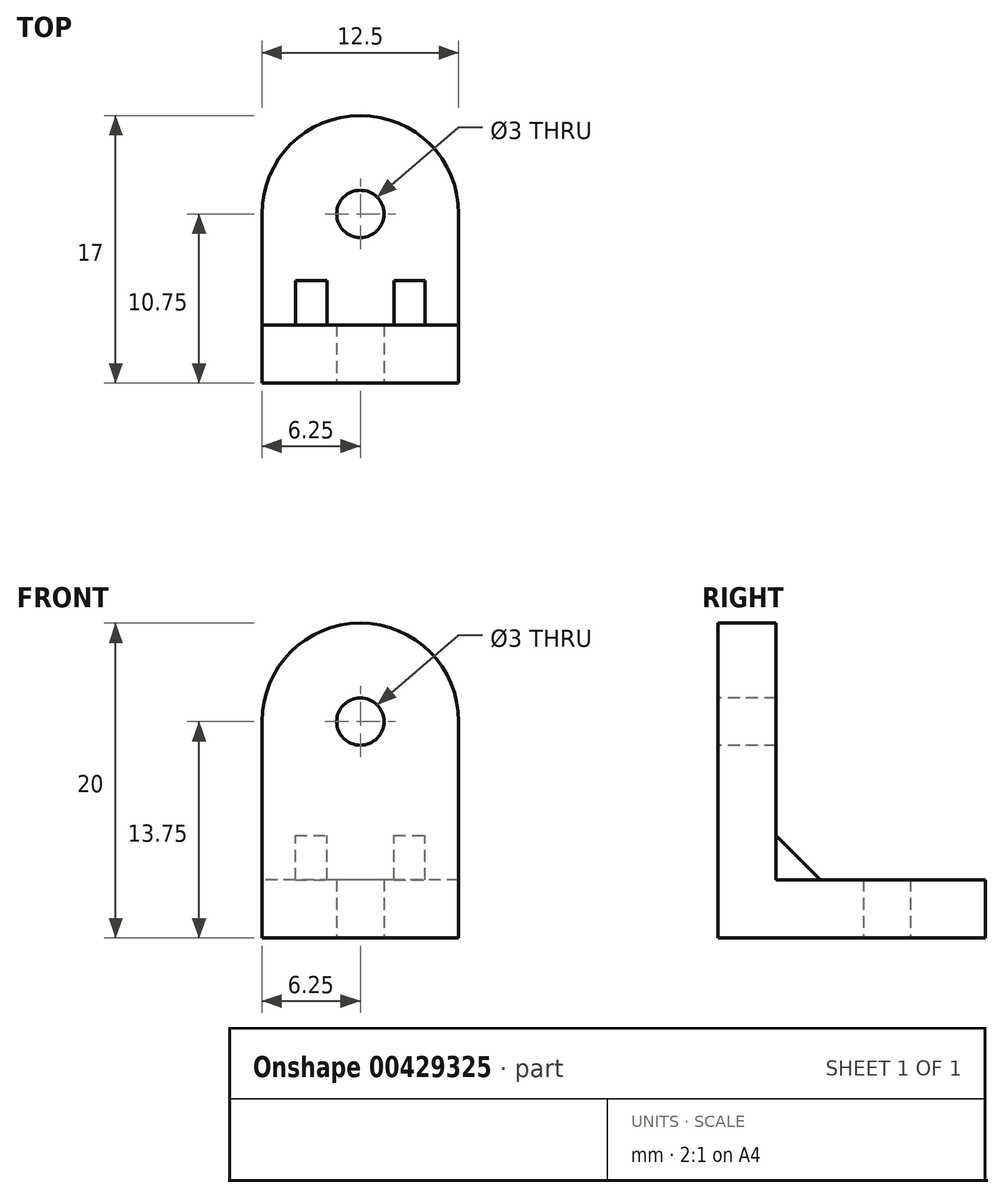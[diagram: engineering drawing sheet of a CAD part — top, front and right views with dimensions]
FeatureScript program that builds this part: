
annotation { "Feature Type Name" : "Feature", "Feature Type Description" : "" }
export const myFeature = defineFeature(function(context is Context, id is Id, definition is map)
    precondition{}
    {
        {
            var Q0;
            Q0=qCreatedBy(makeId("Front.planeOp"),FACE);
            var sketch = newSketch(context, id + "F0", { "sketchPlane" : qUnion([Q0])});
            skLineSegment(sketch, "E0.bottom", {"start": v(0, 0) * mm, "end": v(12.5, 0) * mm});
            skLineSegment(sketch, "E0.top", {"start": v(6.25, 20) * mm, "end": v(6.25, 20) * mm});
            skLineSegment(sketch, "E0.left", {"start": v(0, 0) * mm, "end": v(0, 13.75) * mm});
            skLineSegment(sketch, "E0.right", {"start": v(12.5, 0) * mm, "end": v(12.5, 13.75) * mm});
            skPoint(sketch, "E1.visualSharp", {"position": v(0, 20) * mm});
            skArc(sketch, "E1.filletArc", {"start": v(6.25, 20) * mm, "mid": v(1.83, 18.17) * mm, "end": v(0, 13.75) * mm});
            skPoint(sketch, "E2.visualSharp", {"position": v(12.5, 20) * mm});
            skArc(sketch, "E2.filletArc", {"start": v(12.5, 13.75) * mm, "mid": v(10.67, 18.17) * mm, "end": v(6.25, 20) * mm});
            skCircle(sketch, "E3", {"center": v(6.25, 13.75) * mm, "radius": 1.5 * mm});
            skSolve(sketch);
        }
        {
            var Q0;
            Q0=qCreatedBy(makeId("Top.planeOp"),FACE);
            var sketch = newSketch(context, id + "F1", { "sketchPlane" : qUnion([Q0])});
            skLineSegment(sketch, "E4.bottom", {"start": v(0, 0) * mm, "end": v(12.5, 0) * mm});
            skLineSegment(sketch, "E4.top", {"start": v(6.25, 17) * mm, "end": v(6.25, 17) * mm});
            skLineSegment(sketch, "E4.left", {"start": v(0, 0) * mm, "end": v(0, 10.75) * mm});
            skLineSegment(sketch, "E4.right", {"start": v(12.5, 0) * mm, "end": v(12.5, 10.75) * mm});
            skPoint(sketch, "E5.visualSharp", {"position": v(0, 17) * mm});
            skArc(sketch, "E5.filletArc", {"start": v(6.25, 17) * mm, "mid": v(1.83, 15.17) * mm, "end": v(0, 10.75) * mm});
            skPoint(sketch, "E6.visualSharp", {"position": v(12.5, 17) * mm});
            skArc(sketch, "E6.filletArc", {"start": v(12.5, 10.75) * mm, "mid": v(10.67, 15.17) * mm, "end": v(6.25, 17) * mm});
            skCircle(sketch, "E7", {"center": v(6.25, 10.75) * mm, "radius": 1.5 * mm});
            skSolve(sketch);
        }
        {
            var Q0;
            Q0=makeQuery(id+"F0.imprint","IMPRINT",FACE,{"disambiguationData":[TD([[makeQuery(id+"F0.imprint","IMPRINT",EDGE,{"derivedFrom":sQuery(id+"F0.wireOp",EDGE,"E0.bottom")}),1.0]])]});
            extrude(context, id + "F2", {"entities" : qUnion([Q0]), "oppositeDirection" : true, "depth" : 3.7 * mm});
        }
        {
            var Q0;
            Q0=makeQuery(id+"F1.imprint","IMPRINT",FACE,{"disambiguationData":[TD([[makeQuery(id+"F1.imprint","IMPRINT",EDGE,{"derivedFrom":sQuery(id+"F1.wireOp",EDGE,"E4.bottom")}),1.0]])]});
            extrude(context, id + "F3", {"entities" : qUnion([Q0]), "operationType" : NewBodyOperationType.ADD, "depth" : 3.7 * mm});
        }
        {
            var Q0;
            Q0=makeQuery(id+"F3.boolean.opBoolean","INTERSECT",EDGE,{"derivedFrom":[makeQuery(id+"F2.opExtrude","CAP_FACE",FACE,{"disambiguationData":[OSD([sQuery(id+"F0.wireOp",EDGE,"E0.bottom"),sQuery(id+"F0.wireOp",EDGE,"E0.left"),sQuery(id+"F0.wireOp",EDGE,"E0.right"),sQuery(id+"F0.wireOp",EDGE,"E1.filletArc"),sQuery(id+"F0.wireOp",EDGE,"E2.filletArc"),sQuery(id+"F0.wireOp",EDGE,"E3")])],"isStart":false}),makeQuery(id+"F3.opExtrude","CAP_FACE",FACE,{"disambiguationData":[OSD([sQuery(id+"F1.wireOp",EDGE,"E4.bottom"),sQuery(id+"F1.wireOp",EDGE,"E4.left"),sQuery(id+"F1.wireOp",EDGE,"E4.right"),sQuery(id+"F1.wireOp",EDGE,"E5.filletArc"),sQuery(id+"F1.wireOp",EDGE,"E6.filletArc"),sQuery(id+"F1.wireOp",EDGE,"E7")])],"isStart":false})]});
            cPlane(context, id + "F4", {"entities" : qUnion([Q0]), "cplaneType" : CPlaneType.LINE_ANGLE, "offset" : 25 * mm, "angle" : 45 * degree, "oppositeDirection" : true, "width" : 150 * mm, "height" : 150 * mm});
        }
        {
            var Q0;
            Q0=qCreatedBy(id+"F4.planeOp",FACE);
            cPlane(context, id + "F5", {"entities" : qUnion([Q0]), "cplaneType" : CPlaneType.OFFSET, "offset" : 2 * mm, "oppositeDirection" : true, "width" : 150 * mm, "height" : 150 * mm});
        }
        {
            var Q0;
            Q0=qCreatedBy(id+"F5.planeOp",FACE);
            var sketch = newSketch(context, id + "F6", { "sketchPlane" : qUnion([Q0])});
            skPoint(sketch, "E8", {"position": v(9.38, 0) * mm});
            skPoint(sketch, "E9", {"position": v(3.12, 0) * mm});
            skLineSegment(sketch, "E10.bottom", {"start": v(8.38, 2) * mm, "end": v(10.38, 2) * mm});
            skLineSegment(sketch, "E10.top", {"start": v(8.38, -2) * mm, "end": v(10.38, -2) * mm});
            skLineSegment(sketch, "E10.left", {"start": v(8.38, 2) * mm, "end": v(8.38, -2) * mm});
            skLineSegment(sketch, "E10.right", {"start": v(10.38, 2) * mm, "end": v(10.38, -2) * mm});
            skLineSegment(sketch, "E11.bottom", {"start": v(2.12, 2) * mm, "end": v(4.13, 2) * mm});
            skLineSegment(sketch, "E11.top", {"start": v(2.12, -2) * mm, "end": v(4.13, -2) * mm});
            skLineSegment(sketch, "E11.left", {"start": v(2.12, 2) * mm, "end": v(2.12, -2) * mm});
            skLineSegment(sketch, "E11.right", {"start": v(4.13, 2) * mm, "end": v(4.13, -2) * mm});
            skLineSegment(sketch, "E12", {"start": v(0, 0) * mm, "end": v(12.5, 0) * mm, "construction": true});
            skLineSegment(sketch, "E13", {"start": v(12.5, -2) * mm, "end": v(0, -2) * mm, "construction": true});
            skLineSegment(sketch, "E14", {"start": v(12.5, 2) * mm, "end": v(0, 2) * mm, "construction": true});
            skSolve(sketch);
        }
        {
            var Q0;
            Q0 = qSketchRegion(id + "F6", true);
            extrude(context, id + "F7", {"entities" : qUnion([Q0]), "operationType" : NewBodyOperationType.ADD, "depth" : 4 * mm});
        }
    });
